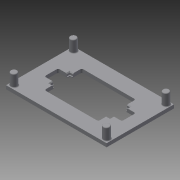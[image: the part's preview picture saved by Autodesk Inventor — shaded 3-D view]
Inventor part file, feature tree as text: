
AUTODESK INVENTOR PART (.ipt)
format: ipt  version: 2013 (Build 170138000, 138)  size: 186,368 bytes
history: native  units: mm
features: extrude x5, sketch x5, fillet x2, chamfer x1
ambient origin geometry x8: Origin, YZ Plane, XZ Plane, XY Plane, X Axis, Y Axis, Z Axis, Center Point
bodies: Solid1 (feature_tree)
feature tree (13):
  extrude  "Extrusion1"  Depth=85.5mm
  extrude  "Extrusion2"  Depth=76.5mm
  extrude  "Extrusion3"  Depth=3.5mm TaperAngle=0.0deg
  chamfer  "Chamfer1"  Distance=3.5mm
  extrude  "Extrusion4"  Depth=8.0mm
  fillet  "Fillet1"  Radius=5.0mm
  extrude  "Extrusion5"  Depth=15.0mm TaperAngle=0.0deg
  fillet  "Fillet2"  Radius=1.0mm
  sketch  "Sketch1"  dims[d0=127.7mm d1=85.5mm]
  sketch  "Sketch2"  dims[d2=4.5mm d3=0.0mm d4=76.5mm]
  sketch  "Sketch3"  dims[d5=25.5mm d6=3.5mm d7=0.0mm]
  sketch  "Sketch4"  dims[d8=1.0mm d10=3.5mm d11=0.0mm]
  sketch  "Sketch5"  dims[d12=1.0mm d13=2.0mm d14=45.0deg d15=8.0mm d17=5.0mm d18=15.0mm d19=0.0mm d20=1.0mm d22=10.0mm d24=5.0mm d25=5.0mm d26=10.0mm d27=10.0mm d28=0.0mm d29=2.0mm]
